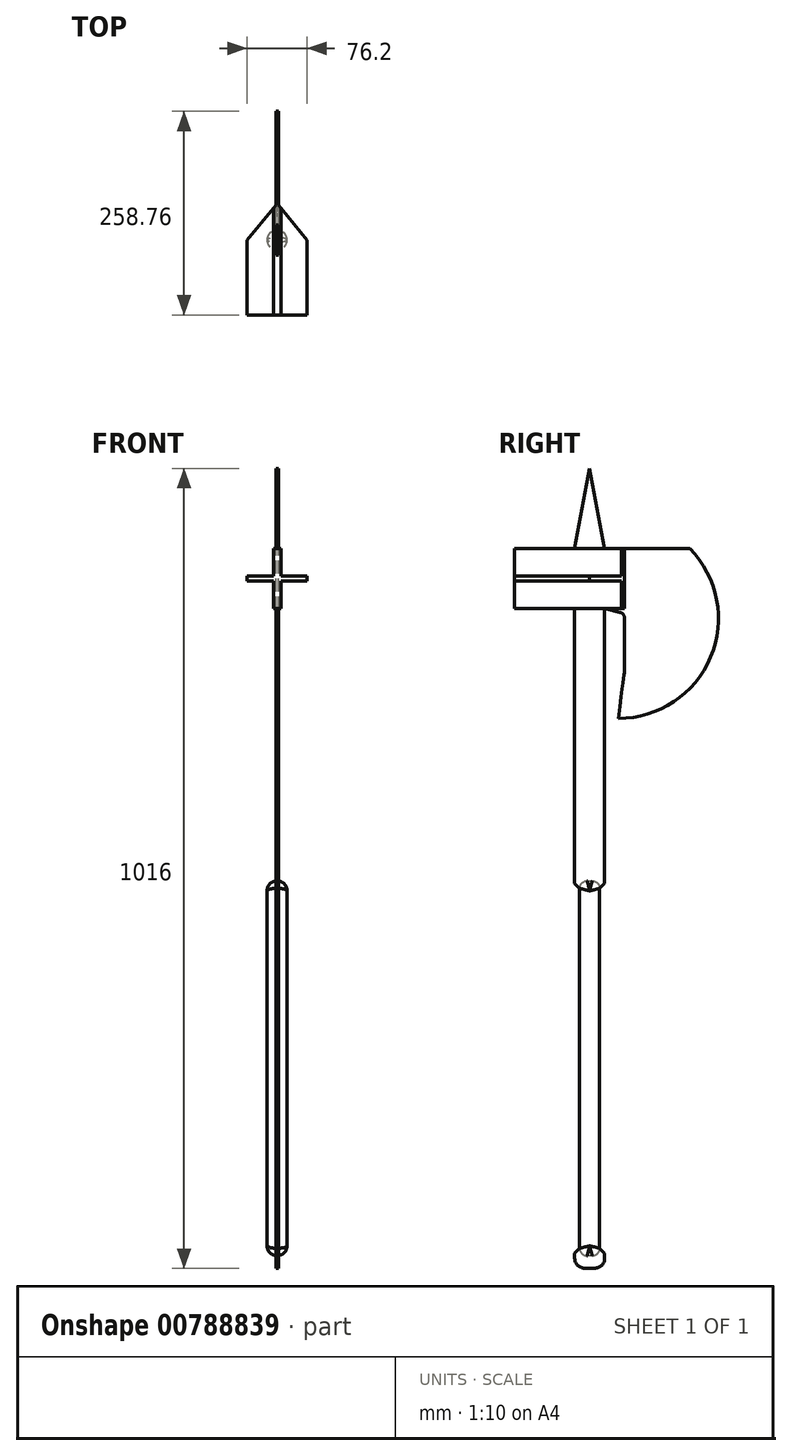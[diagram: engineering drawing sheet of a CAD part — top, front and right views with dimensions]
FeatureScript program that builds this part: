
annotation { "Feature Type Name" : "Feature", "Feature Type Description" : "" }
export const myFeature = defineFeature(function(context is Context, id is Id, definition is map)
    precondition{}
    {
        {
            var Q0;
            Q0=qCreatedBy(makeId("Front.planeOp"),FACE);
            var sketch = newSketch(context, id + "F0", { "sketchPlane" : qUnion([Q0])});
            skLineSegment(sketch, "E0.bottom", {"start": v(1.59, 0) * mm, "end": v(-1.59, 0) * mm});
            skLineSegment(sketch, "E0.top", {"start": v(1.59, 914.4) * mm, "end": v(-1.59, 914.4) * mm});
            skLineSegment(sketch, "E0.left", {"start": v(1.59, 0) * mm, "end": v(1.59, 914.4) * mm});
            skLineSegment(sketch, "E0.right", {"start": v(-1.59, 0) * mm, "end": v(-1.59, 914.4) * mm});
            skPoint(sketch, "E0.middle", {"position": v(0, 457.2) * mm});
            skLineSegment(sketch, "E1.bottom", {"start": v(4.76, 838.2) * mm, "end": v(-4.76, 838.2) * mm});
            skLineSegment(sketch, "E1.top", {"start": v(4.76, 914.4) * mm, "end": v(-4.76, 914.4) * mm});
            skLineSegment(sketch, "E1.left", {"start": v(4.76, 838.2) * mm, "end": v(4.76, 914.4) * mm});
            skLineSegment(sketch, "E1.right", {"start": v(-4.76, 838.2) * mm, "end": v(-4.76, 914.4) * mm});
            skPoint(sketch, "E1.middle", {"position": v(0, 876.3) * mm});
            skLineSegment(sketch, "E2.bottom", {"start": v(38.1, 873.13) * mm, "end": v(-38.1, 873.13) * mm});
            skLineSegment(sketch, "E2.top", {"start": v(38.1, 879.48) * mm, "end": v(-38.1, 879.48) * mm});
            skLineSegment(sketch, "E2.left", {"start": v(38.1, 873.13) * mm, "end": v(38.1, 879.48) * mm});
            skLineSegment(sketch, "E2.right", {"start": v(-38.1, 873.13) * mm, "end": v(-38.1, 879.48) * mm});
            skSolve(sketch);
        }
        {
            var Q0;
            {var subQ0=sQuery(id+"F0.wireOp",EDGE,"E0.bottom");Q0=makeQuery(id+"F0.imprint","IMPRINT",FACE,{"disambiguationData":[TD([[makeQuery(id+"F0.imprint","IMPRINT",EDGE,{"derivedFrom":subQ0}),-1.0]])]});}
            extrude(context, id + "F1", {"entities" : qUnion([Q0]), "depth" : 19.05 * mm, "offsetDistance" : 25.4 * mm, "hasSecondDirection" : true, "secondDirectionOppositeDirection" : true, "secondDirectionDepth" : 19.05 * mm});
        }
        {
            var Q0;
            {var subQ5=sQuery(id+"F0.wireOp",EDGE,"E2.left");Q0=makeQuery(id+"F0.imprint","IMPRINT",FACE,{"disambiguationData":[TD([[makeQuery(id+"F0.imprint","IMPRINT",EDGE,{"derivedFrom":subQ5}),1.0]])]});}
            var Q1;
            {var subQ0=sQuery(id+"F0.wireOp",EDGE,"E1.bottom");var subQ1=sQuery(id+"F0.wireOp",EDGE,"E0.left");var subQ2=makeQuery(id+"F0.imprint","INTERSECT",VERTEX,{"derivedFrom":[subQ1,subQ0]});Q1=makeQuery(id+"F0.imprint","IMPRINT",FACE,{"disambiguationData":[TD([[makeQuery(id+"F0.imprint","IMPRINT",EDGE,{"disambiguationData":[TD([[subQ2,-1.0]])],"derivedFrom":subQ1}),-1.0]])]});}
            var Q2;
            {var subQ0=sQuery(id+"F0.wireOp",EDGE,"E1.bottom");var subQ1=sQuery(id+"F0.wireOp",EDGE,"E0.right");var subQ2=makeQuery(id+"F0.imprint","INTERSECT",VERTEX,{"derivedFrom":[subQ1,subQ0]});Q2=makeQuery(id+"F0.imprint","IMPRINT",FACE,{"disambiguationData":[TD([[makeQuery(id+"F0.imprint","IMPRINT",EDGE,{"disambiguationData":[TD([[subQ2,-1.0]])],"derivedFrom":subQ1}),1.0]])]});}
            var Q3;
            {var subQ0=sQuery(id+"F0.wireOp",EDGE,"E2.bottom");var subQ1=sQuery(id+"F0.wireOp",EDGE,"E0.right");var subQ2=makeQuery(id+"F0.imprint","INTERSECT",VERTEX,{"derivedFrom":[subQ1,subQ0]});Q3=makeQuery(id+"F0.imprint","IMPRINT",FACE,{"disambiguationData":[TD([[makeQuery(id+"F0.imprint","IMPRINT",EDGE,{"disambiguationData":[TD([[subQ2,-1.0]])],"derivedFrom":subQ1}),1.0]])]});}
            var Q4;
            {var subQ5=sQuery(id+"F0.wireOp",EDGE,"E2.right");Q4=makeQuery(id+"F0.imprint","IMPRINT",FACE,{"disambiguationData":[TD([[makeQuery(id+"F0.imprint","IMPRINT",EDGE,{"derivedFrom":subQ5}),-1.0]])]});}
            var Q5;
            {var subQ0=sQuery(id+"F0.wireOp",EDGE,"E1.top");var subQ1=sQuery(id+"F0.wireOp",EDGE,"E0.right");var subQ2=makeQuery(id+"F0.imprint","INTERSECT",VERTEX,{"derivedFrom":[subQ1,subQ0]});Q5=makeQuery(id+"F0.imprint","IMPRINT",FACE,{"disambiguationData":[TD([[makeQuery(id+"F0.imprint","IMPRINT",EDGE,{"disambiguationData":[TD([[subQ2,1.0]])],"derivedFrom":subQ1}),1.0]])]});}
            var Q6;
            {var subQ0=sQuery(id+"F0.wireOp",EDGE,"E1.top");var subQ1=sQuery(id+"F0.wireOp",EDGE,"E0.left");var subQ2=makeQuery(id+"F0.imprint","INTERSECT",VERTEX,{"derivedFrom":[subQ1,subQ0]});Q6=makeQuery(id+"F0.imprint","IMPRINT",FACE,{"disambiguationData":[TD([[makeQuery(id+"F0.imprint","IMPRINT",EDGE,{"disambiguationData":[TD([[subQ2,1.0]])],"derivedFrom":subQ1}),-1.0]])]});}
            var Q7;
            {var subQ0=sQuery(id+"F0.wireOp",EDGE,"E2.bottom");var subQ1=sQuery(id+"F0.wireOp",EDGE,"E0.left");var subQ2=makeQuery(id+"F0.imprint","INTERSECT",VERTEX,{"derivedFrom":[subQ1,subQ0]});Q7=makeQuery(id+"F0.imprint","IMPRINT",FACE,{"disambiguationData":[TD([[makeQuery(id+"F0.imprint","IMPRINT",EDGE,{"disambiguationData":[TD([[subQ2,-1.0]])],"derivedFrom":subQ1}),-1.0]])]});}
            var Q8;
            {var subQ0=sQuery(id+"F0.wireOp",EDGE,"E1.top");var subQ1=sQuery(id+"F0.wireOp",EDGE,"E0.left");var subQ2=makeQuery(id+"F0.imprint","INTERSECT",VERTEX,{"derivedFrom":[subQ1,subQ0]});Q8=makeQuery(id+"F0.imprint","IMPRINT",FACE,{"disambiguationData":[TD([[makeQuery(id+"F0.imprint","IMPRINT",EDGE,{"disambiguationData":[TD([[subQ2,1.0]])],"derivedFrom":subQ1}),1.0]])]});}
            var Q9;
            {var subQ0=sQuery(id+"F0.wireOp",EDGE,"E2.bottom");var subQ1=sQuery(id+"F0.wireOp",EDGE,"E0.left");var subQ2=makeQuery(id+"F0.imprint","INTERSECT",VERTEX,{"derivedFrom":[subQ1,subQ0]});Q9=makeQuery(id+"F0.imprint","IMPRINT",FACE,{"disambiguationData":[TD([[makeQuery(id+"F0.imprint","IMPRINT",EDGE,{"disambiguationData":[TD([[subQ2,-1.0]])],"derivedFrom":subQ1}),1.0]])]});}
            var Q10;
            {var subQ0=sQuery(id+"F0.wireOp",EDGE,"E1.bottom");var subQ1=sQuery(id+"F0.wireOp",EDGE,"E0.left");var subQ2=makeQuery(id+"F0.imprint","INTERSECT",VERTEX,{"derivedFrom":[subQ1,subQ0]});Q10=makeQuery(id+"F0.imprint","IMPRINT",FACE,{"disambiguationData":[TD([[makeQuery(id+"F0.imprint","IMPRINT",EDGE,{"disambiguationData":[TD([[subQ2,-1.0]])],"derivedFrom":subQ1}),1.0]])]});}
            extrude(context, id + "F2", {"entities" : qUnion([Q0, Q1, Q2, Q3, Q4, Q5, Q6, Q7, Q8, Q9, Q10]), "operationType" : NewBodyOperationType.ADD, "depth" : 95.25 * mm, "offsetDistance" : 25.4 * mm, "hasSecondDirection" : true, "secondDirectionOppositeDirection" : true, "secondDirectionDepth" : 44.45 * mm});
        }
        {
            var Q0;
            Q0=qCreatedBy(makeId("Right.planeOp"),FACE);
            var sketch = newSketch(context, id + "F3", { "sketchPlane" : qUnion([Q0])});
            skCircle(sketch, "E3", {"center": v(36.51, 825.5) * mm, "radius": 127 * mm});
            skLineSegment(sketch, "E4", {"start": v(-54.18, 914.4) * mm, "end": v(127.2, 914.4) * mm});
            skLineSegment(sketch, "E5", {"start": v(0, 1017.32) * mm, "end": v(0, 715.22) * mm, "construction": true});
            skCircle(sketch, "E6", {"center": v(36.51, 825.5) * mm, "radius": 7.94 * mm});
            skLineSegment(sketch, "E7", {"start": v(19.05, 838.2) * mm, "end": v(38.5, 833.19) * mm});
            skLineSegment(sketch, "E8", {"start": v(36.51, 825.5) * mm, "end": v(36.51, 698.5) * mm, "construction": true});
            skPoint(sketch, "E9.start.orphan", {"position": v(44.45, 825.5) * mm});
            skFitSpline(sketch, "E10", {"points": [v(44.45, 825.5) * mm, v(44.45, 762) * mm, v(36.51, 698.5) * mm], "startDerivative": vector(0, -307.89) * mm, "endDerivative": vector(-47.53, -380.26) * mm});
            skPoint(sketch, "E11", {"position": v(36.51, 817.56) * mm});
            skLineSegment(sketch, "E12", {"start": v(19.05, 838.2) * mm, "end": v(19.05, 914.4) * mm});
            skSolve(sketch);
        }
        {
            var Q0;
            {var subQ0=sQuery(id+"F3.wireOp",EDGE,"E7");Q0=makeQuery(id+"F3.imprint","IMPRINT",FACE,{"disambiguationData":[TD([[makeQuery(id+"F3.imprint","IMPRINT",EDGE,{"derivedFrom":subQ0}),1.0]])]});}
            extrude(context, id + "F4", {"entities" : qUnion([Q0]), "operationType" : NewBodyOperationType.ADD, "depth" : 1.59 * mm, "offsetDistance" : 25.4 * mm, "hasSecondDirection" : true, "secondDirectionOppositeDirection" : true, "secondDirectionDepth" : 1.59 * mm});
        }
        {
            var Q0;
            Q0=qCreatedBy(makeId("Top.planeOp"),FACE);
            var sketch = newSketch(context, id + "F5", { "sketchPlane" : qUnion([Q0])});
            skLineSegment(sketch, "E13", {"start": v(1.59, 44.45) * mm, "end": v(38.1, 0) * mm});
            skLineSegment(sketch, "E14", {"start": v(-1.59, 44.45) * mm, "end": v(-38.1, 0) * mm});
            skLineSegment(sketch, "E15", {"start": v(1.59, 44.45) * mm, "end": v(38.1, 44.45) * mm});
            skLineSegment(sketch, "E16", {"start": v(38.1, 44.45) * mm, "end": v(38.1, 0) * mm});
            skLineSegment(sketch, "E17", {"start": v(-1.59, 44.45) * mm, "end": v(-38.1, 44.45) * mm});
            skLineSegment(sketch, "E18", {"start": v(-38.1, 44.45) * mm, "end": v(-38.1, 0) * mm});
            skSolve(sketch);
        }
        {
            var Q0;
            Q0 = qSketchRegion(id + "F5", true);
            extrude(context, id + "F6", {"entities" : qUnion([Q0]), "operationType" : NewBodyOperationType.REMOVE, "depth" : 1016 * mm, "offsetDistance" : 25.4 * mm});
        }
        {
            var Q0;
            Q0=qCreatedBy(makeId("Right.planeOp"),FACE);
            var sketch = newSketch(context, id + "F7", { "sketchPlane" : qUnion([Q0])});
            skLineSegment(sketch, "E19.bottom", {"start": v(6.35, 0) * mm, "end": v(-6.35, 0) * mm});
            skLineSegment(sketch, "E19.top", {"start": v(19.05, 25.4) * mm, "end": v(-19.05, 25.4) * mm, "construction": true});
            skLineSegment(sketch, "E19.left", {"start": v(19.05, 12.7) * mm, "end": v(19.05, 25.4) * mm});
            skLineSegment(sketch, "E19.right", {"start": v(-19.05, 12.7) * mm, "end": v(-19.05, 25.4) * mm});
            skPoint(sketch, "E19.middle", {"position": v(0, 12.7) * mm});
            skPoint(sketch, "E20.visualSharp", {"position": v(19.05, 0) * mm});
            skPoint(sketch, "E21.visualSharp", {"position": v(-19.05, 0) * mm});
            skLineSegment(sketch, "E22", {"start": v(25.4, 12.7) * mm, "end": v(12.7, 25.4) * mm});
            skLineSegment(sketch, "E23", {"start": v(12.7, 25.4) * mm, "end": v(12.7, 482.6) * mm});
            skLineSegment(sketch, "E24", {"start": v(12.7, 482.6) * mm, "end": v(25.4, 495.3) * mm});
            skLineSegment(sketch, "E25", {"start": v(25.4, 495.3) * mm, "end": v(25.4, 12.7) * mm});
            skPoint(sketch, "E26.end.orphan", {"position": v(-19.05, 15.64) * mm});
            skArc(sketch, "E27.filletArc", {"start": v(-19.05, 12.7) * mm, "mid": v(-15.33, 3.72) * mm, "end": v(-6.35, 0) * mm});
            skLineSegment(sketch, "E28", {"start": v(-19.05, 12.7) * mm, "end": v(-19.05, 0) * mm});
            skLineSegment(sketch, "E29", {"start": v(-19.05, 0) * mm, "end": v(-6.35, 0) * mm});
            skPoint(sketch, "E30.end.orphan", {"position": v(-6.35, 0) * mm});
            skArc(sketch, "E31.filletArc", {"start": v(6.35, 0) * mm, "mid": v(15.33, 3.72) * mm, "end": v(19.05, 12.7) * mm});
            skLineSegment(sketch, "E32", {"start": v(19.05, 12.7) * mm, "end": v(19.05, 0) * mm});
            skLineSegment(sketch, "E33", {"start": v(19.05, 0) * mm, "end": v(6.35, 0) * mm});
            skLineSegment(sketch, "E34", {"start": v(-12.7, 25.4) * mm, "end": v(-12.7, 482.6) * mm});
            skLineSegment(sketch, "E35", {"start": v(-12.7, 482.6) * mm, "end": v(-25.4, 495.3) * mm});
            skLineSegment(sketch, "E36", {"start": v(-25.4, 495.3) * mm, "end": v(-25.4, 12.7) * mm});
            skLineSegment(sketch, "E37", {"start": v(-25.4, 12.7) * mm, "end": v(-12.7, 25.4) * mm});
            skSolve(sketch);
        }
        {
            var Q0;
            Q0 = qSketchRegion(id + "F7", true);
            extrude(context, id + "F8", {"entities" : qUnion([Q0]), "operationType" : NewBodyOperationType.REMOVE, "oppositeDirection" : true, "depth" : 25.4 * mm, "offsetDistance" : 25.4 * mm, "hasSecondDirection" : true, "secondDirectionOppositeDirection" : false, "secondDirectionDepth" : 25.4 * mm});
        }
        {
            var Q0;
            Q0=qCreatedBy(makeId("Right.planeOp"),FACE);
            var sketch = newSketch(context, id + "F9", { "sketchPlane" : qUnion([Q0])});
            skLineSegment(sketch, "E38.bottom", {"start": v(-3.18, 492.13) * mm, "end": v(3.17, 492.13) * mm});
            skLineSegment(sketch, "E38.top", {"start": v(-3.17, 15.88) * mm, "end": v(3.18, 15.88) * mm});
            skLineSegment(sketch, "E38.left", {"start": v(-12.7, 482.6) * mm, "end": v(-12.7, 25.4) * mm});
            skLineSegment(sketch, "E38.right", {"start": v(12.7, 482.6) * mm, "end": v(12.7, 25.4) * mm});
            skPoint(sketch, "E39.visualSharp", {"position": v(-12.7, 492.13) * mm});
            skArc(sketch, "E39.filletArc", {"start": v(-3.18, 492.13) * mm, "mid": v(-9.91, 489.34) * mm, "end": v(-12.7, 482.6) * mm});
            skPoint(sketch, "E40.visualSharp", {"position": v(12.7, 492.13) * mm});
            skArc(sketch, "E40.filletArc", {"start": v(12.7, 482.6) * mm, "mid": v(9.91, 489.34) * mm, "end": v(3.17, 492.13) * mm});
            skPoint(sketch, "E41.visualSharp", {"position": v(12.7, 15.87) * mm});
            skArc(sketch, "E41.filletArc", {"start": v(3.18, 15.87) * mm, "mid": v(9.91, 18.66) * mm, "end": v(12.7, 25.4) * mm});
            skPoint(sketch, "E42.visualSharp", {"position": v(-12.7, 15.88) * mm});
            skArc(sketch, "E42.filletArc", {"start": v(-12.7, 25.4) * mm, "mid": v(-9.91, 18.66) * mm, "end": v(-3.17, 15.88) * mm});
            skSolve(sketch);
        }
        {
            var Q0;
            Q0 = qSketchRegion(id + "F9", true);
            extrude(context, id + "F10", {"entities" : qUnion([Q0]), "depth" : 12.7 * mm, "offsetDistance" : 25.4 * mm, "hasSecondDirection" : true, "secondDirectionOppositeDirection" : true, "secondDirectionDepth" : 12.7 * mm});
        }
        {
            var Q0;
            Q0=makeQuery(id+"F10.opExtrude","CAP_FACE",FACE,{"disambiguationData":[OSD([sQuery(id+"F9.wireOp",EDGE,"E38.bottom"),sQuery(id+"F9.wireOp",EDGE,"E38.top"),sQuery(id+"F9.wireOp",EDGE,"E38.left"),sQuery(id+"F9.wireOp",EDGE,"E38.right"),sQuery(id+"F9.wireOp",EDGE,"E39.filletArc"),sQuery(id+"F9.wireOp",EDGE,"E40.filletArc"),sQuery(id+"F9.wireOp",EDGE,"E41.filletArc"),sQuery(id+"F9.wireOp",EDGE,"E42.filletArc")])],"isStart":false});
            var Q1;
            Q1=makeQuery(id+"F10.opExtrude","CAP_FACE",FACE,{"disambiguationData":[OSD([sQuery(id+"F9.wireOp",EDGE,"E38.bottom"),sQuery(id+"F9.wireOp",EDGE,"E38.top"),sQuery(id+"F9.wireOp",EDGE,"E38.left"),sQuery(id+"F9.wireOp",EDGE,"E38.right"),sQuery(id+"F9.wireOp",EDGE,"E39.filletArc"),sQuery(id+"F9.wireOp",EDGE,"E40.filletArc"),sQuery(id+"F9.wireOp",EDGE,"E41.filletArc"),sQuery(id+"F9.wireOp",EDGE,"E42.filletArc")])],"isStart":true});
            fillet(context, id + "F11", {"entities" : qUnion([Q0, Q1]), "radius" : 12.7 * mm, "tangentPropagation" : true, "allowEdgeOverflow" : false});
        }
        {
            var Q0;
            Q0=qCreatedBy(makeId("Right.planeOp"),FACE);
            var sketch = newSketch(context, id + "F12", { "sketchPlane" : qUnion([Q0])});
            skLineSegment(sketch, "E43.bottom", {"start": v(19.05, 889) * mm, "end": v(-19.05, 889) * mm});
            skLineSegment(sketch, "E43.left", {"start": v(19.05, 889) * mm, "end": v(19.05, 914.4) * mm});
            skLineSegment(sketch, "E43.right", {"start": v(-19.05, 889) * mm, "end": v(-19.05, 914.4) * mm});
            skPoint(sketch, "E43.middle", {"position": v(0, 952.5) * mm});
            skLineSegment(sketch, "E44", {"start": v(0, 1016) * mm, "end": v(-19.05, 914.4) * mm});
            skLineSegment(sketch, "E45", {"start": v(0, 1016) * mm, "end": v(19.05, 914.4) * mm});
            skPoint(sketch, "E46.orphan", {"position": v(19.05, 1016) * mm});
            skPoint(sketch, "E47.orphan", {"position": v(-19.05, 1016) * mm});
            skSolve(sketch);
        }
        {
            var Q0;
            Q0 = qSketchRegion(id + "F12", true);
            extrude(context, id + "F13", {"entities" : qUnion([Q0]), "operationType" : NewBodyOperationType.ADD, "depth" : 1.59 * mm, "offsetDistance" : 25.4 * mm, "hasSecondDirection" : true, "secondDirectionOppositeDirection" : true, "secondDirectionDepth" : 1.59 * mm});
        }
    });
